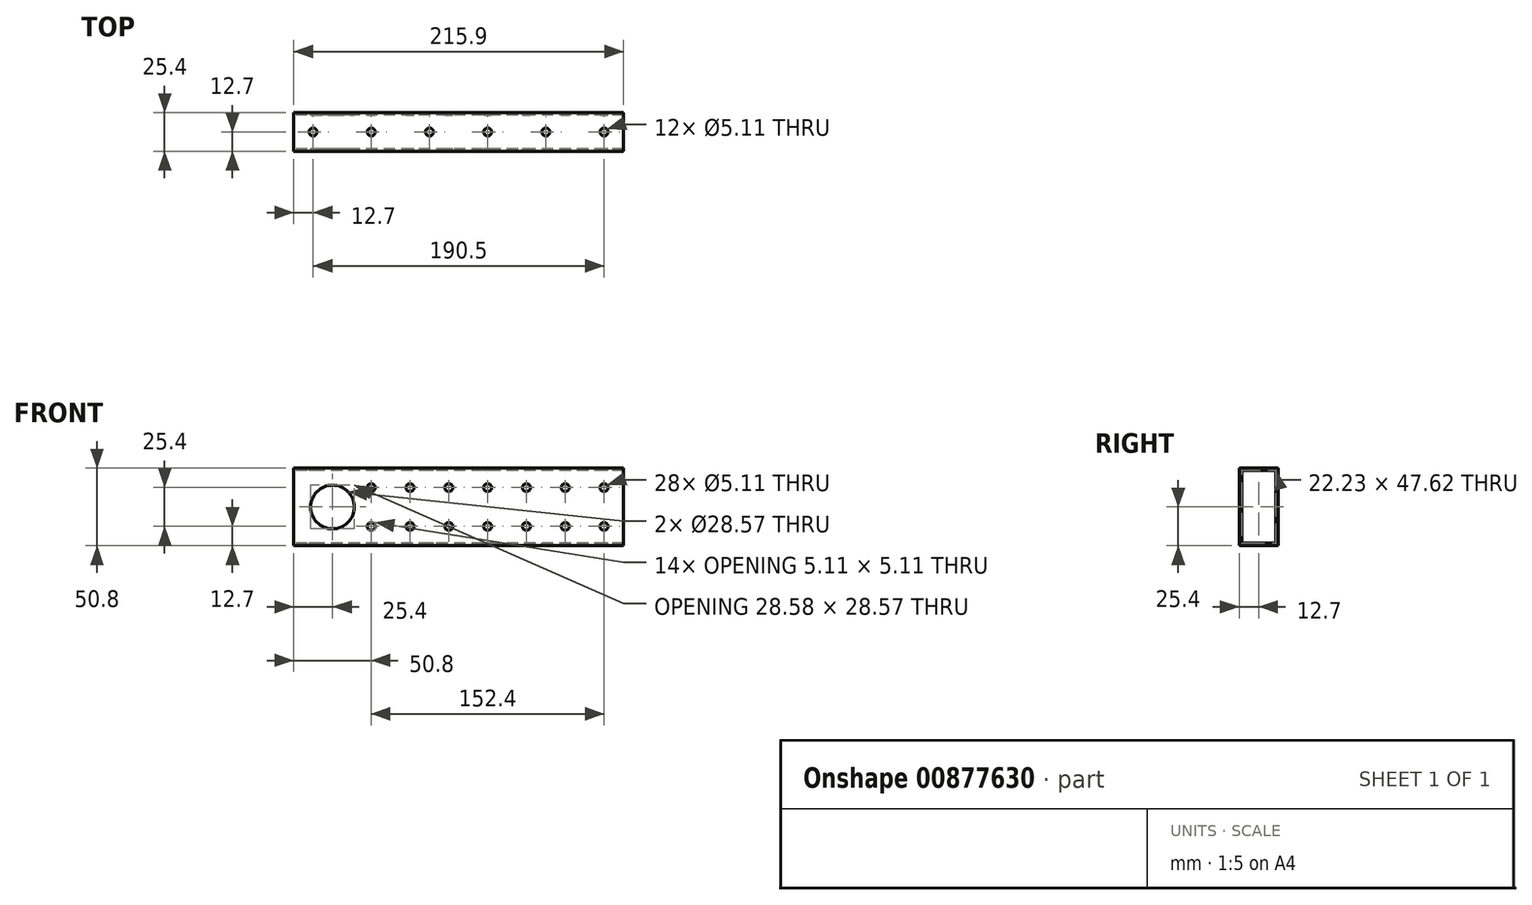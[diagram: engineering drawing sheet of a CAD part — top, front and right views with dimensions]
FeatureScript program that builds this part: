
annotation { "Feature Type Name" : "Feature", "Feature Type Description" : "" }
export const myFeature = defineFeature(function(context is Context, id is Id, definition is map)
    precondition{}
    {
        {
            var Q0;
            Q0=qCreatedBy(makeId("Front.planeOp"),FACE);
            var sketch = newSketch(context, id + "F0", { "sketchPlane" : qUnion([Q0])});
            skLineSegment(sketch, "E0.bottom", {"start": v(-107.95, 25.4) * mm, "end": v(107.95, 25.4) * mm});
            skLineSegment(sketch, "E0.top", {"start": v(-107.95, -25.4) * mm, "end": v(107.95, -25.4) * mm});
            skLineSegment(sketch, "E0.left", {"start": v(-107.95, 25.4) * mm, "end": v(-107.95, -25.4) * mm});
            skLineSegment(sketch, "E0.right", {"start": v(107.95, 25.4) * mm, "end": v(107.95, -25.4) * mm});
            skPoint(sketch, "E0.middle", {"position": v(0, 0) * mm});
            skCircle(sketch, "E1", {"center": v(-82.55, 0) * mm, "radius": 41.28 * mm, "construction": true});
            skCircle(sketch, "E2", {"center": v(-82.55, 0) * mm, "radius": 14.29 * mm});
            skCircle(sketch, "E3", {"center": v(95.25, 12.7) * mm, "radius": 2.55 * mm});
            skCircle(sketch, "E4.0.1.0", {"center": v(95.25, -12.7) * mm, "radius": 2.55 * mm});
            skCircle(sketch, "E4.1.0.0", {"center": v(69.85, 12.7) * mm, "radius": 2.55 * mm});
            skCircle(sketch, "E4.1.1.0", {"center": v(69.85, -12.7) * mm, "radius": 2.55 * mm});
            skCircle(sketch, "E4.2.0.0", {"center": v(44.45, 12.7) * mm, "radius": 2.55 * mm});
            skCircle(sketch, "E4.2.1.0", {"center": v(44.45, -12.7) * mm, "radius": 2.55 * mm});
            skCircle(sketch, "E4.3.0.0", {"center": v(19.05, 12.7) * mm, "radius": 2.55 * mm});
            skCircle(sketch, "E4.3.1.0", {"center": v(19.05, -12.7) * mm, "radius": 2.55 * mm});
            skCircle(sketch, "E4.4.0.0", {"center": v(-6.35, 12.7) * mm, "radius": 2.55 * mm});
            skCircle(sketch, "E4.4.1.0", {"center": v(-6.35, -12.7) * mm, "radius": 2.55 * mm});
            skCircle(sketch, "E4.5.0.0", {"center": v(-31.75, 12.7) * mm, "radius": 2.55 * mm});
            skCircle(sketch, "E4.5.1.0", {"center": v(-31.75, -12.7) * mm, "radius": 2.55 * mm});
            skCircle(sketch, "E4.6.0.0", {"center": v(-57.15, 12.7) * mm, "radius": 2.55 * mm});
            skCircle(sketch, "E4.6.1.0", {"center": v(-57.15, -12.7) * mm, "radius": 2.55 * mm});
            skLineSegment(sketch, "E4.direction1", {"start": v(95.25, 12.7) * mm, "end": v(69.85, 12.7) * mm, "construction": true});
            skLineSegment(sketch, "E4.direction2", {"start": v(95.25, 12.7) * mm, "end": v(95.25, -12.7) * mm, "construction": true});
            skSolve(sketch);
        }
        {
            var Q0;
            Q0 = qSketchRegion(id + "F0", true);
            extrude(context, id + "F1", {"entities" : qUnion([Q0]), "depth" : 25.4 * mm, "offsetDistance" : 25.4 * mm});
        }
        {
            var Q0;
            Q0=makeQuery(id+"F1.opExtrude","SWEPT_FACE",FACE,{"disambiguationData":[OSD([sQuery(id+"F0.wireOp",EDGE,"E0.left")])]});
            var sketch = newSketch(context, id + "F2", { "sketchPlane" : qUnion([Q0])});
            skLineSegment(sketch, "E5.bottom", {"start": v(23.81, 23.81) * mm, "end": v(1.59, 23.81) * mm});
            skLineSegment(sketch, "E5.top", {"start": v(23.81, -23.81) * mm, "end": v(1.59, -23.81) * mm});
            skLineSegment(sketch, "E5.left", {"start": v(23.81, 23.81) * mm, "end": v(23.81, -23.81) * mm});
            skLineSegment(sketch, "E5.right", {"start": v(1.59, 23.81) * mm, "end": v(1.59, -23.81) * mm});
            skPoint(sketch, "E5.middle", {"position": v(12.7, 0) * mm});
            skPoint(sketch, "E5.middle.positionSnap0", {"position": v(12.7, 25.4) * mm});
            skPoint(sketch, "E5.centerSnap0", {"position": v(12.7, 25.4) * mm});
            skSolve(sketch);
        }
        {
            var Q0;
            Q0 = qSketchRegion(id + "F2", true);
            extrude(context, id + "F3", {"entities" : qUnion([Q0]), "operationType" : NewBodyOperationType.REMOVE, "endBound" : BoundingType.THROUGH_ALL, "oppositeDirection" : true, "depth" : 25.4 * mm, "offsetDistance" : 25.4 * mm});
        }
        {
            var Q0;
            Q0=makeQuery(id+"F1.opExtrude","SWEPT_FACE",FACE,{"disambiguationData":[OSD([sQuery(id+"F0.wireOp",EDGE,"E0.bottom")])]});
            var sketch = newSketch(context, id + "F4", { "sketchPlane" : qUnion([Q0])});
            skCircle(sketch, "E6", {"center": v(-95.25, -12.7) * mm, "radius": 2.55 * mm});
            skPoint(sketch, "E6.centerSnap0", {"position": v(-107.95, -12.7) * mm});
            skCircle(sketch, "E7.1.0.0", {"center": v(-57.15, -12.7) * mm, "radius": 2.55 * mm});
            skCircle(sketch, "E7.2.0.0", {"center": v(-19.05, -12.7) * mm, "radius": 2.55 * mm});
            skCircle(sketch, "E7.3.0.0", {"center": v(19.05, -12.7) * mm, "radius": 2.55 * mm});
            skCircle(sketch, "E7.4.0.0", {"center": v(57.15, -12.7) * mm, "radius": 2.55 * mm});
            skCircle(sketch, "E7.5.0.0", {"center": v(95.25, -12.7) * mm, "radius": 2.55 * mm});
            skLineSegment(sketch, "E7.direction1", {"start": v(-95.25, -12.7) * mm, "end": v(-57.15, -12.7) * mm, "construction": true});
            skSolve(sketch);
        }
        {
            var Q0;
            Q0 = qSketchRegion(id + "F4", true);
            extrude(context, id + "F5", {"entities" : qUnion([Q0]), "operationType" : NewBodyOperationType.REMOVE, "endBound" : BoundingType.THROUGH_ALL, "oppositeDirection" : true, "depth" : 25.4 * mm, "offsetDistance" : 25.4 * mm});
        }
    });
